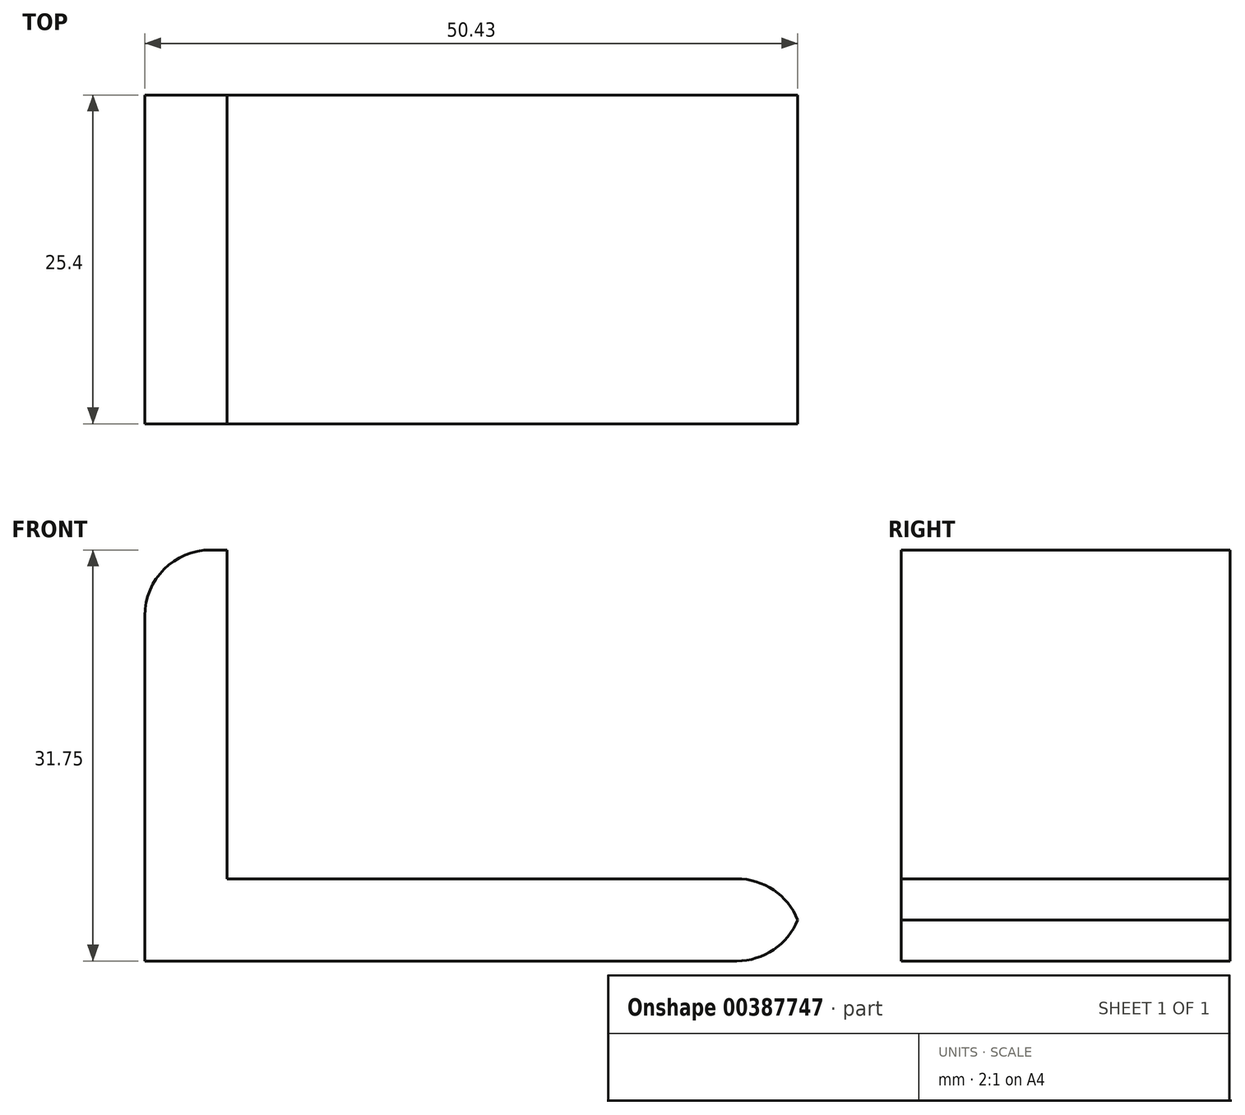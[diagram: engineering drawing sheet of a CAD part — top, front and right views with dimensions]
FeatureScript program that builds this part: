
annotation { "Feature Type Name" : "Feature", "Feature Type Description" : "" }
export const myFeature = defineFeature(function(context is Context, id is Id, definition is map)
    precondition{}
    {
        {
            var Q0;
            Q0=qCreatedBy(makeId("Front.planeOp"),FACE);
            var sketch = newSketch(context, id + "F0", { "sketchPlane" : qUnion([Q0])});
            skLineSegment(sketch, "E0.bottom", {"start": v(0, 0) * mm, "end": v(50.8, 0) * mm});
            skLineSegment(sketch, "E0.left", {"start": v(0, 0) * mm, "end": v(0, 31.75) * mm});
            skLineSegment(sketch, "E1", {"start": v(50.8, 0) * mm, "end": v(50.8, 6.35) * mm});
            skLineSegment(sketch, "E2", {"start": v(50.8, 6.35) * mm, "end": v(6.35, 6.35) * mm});
            skLineSegment(sketch, "E3", {"start": v(6.35, 6.35) * mm, "end": v(6.35, 31.75) * mm});
            skLineSegment(sketch, "E4", {"start": v(0, 31.75) * mm, "end": v(6.35, 31.75) * mm});
            skSolve(sketch);
        }
        {
            var Q0;
            Q0=makeQuery(id+"F0.imprint","IMPRINT",FACE,{"disambiguationData":[TD([[makeQuery(id+"F0.imprint","IMPRINT",EDGE,{"derivedFrom":sQuery(id+"F0.wireOp",EDGE,"E0.bottom")}),1.0]])]});
            extrude(context, id + "F1", {"entities" : qUnion([Q0]), "oppositeDirection" : true, "depth" : 25.4 * mm});
        }
        {
            var Q0;
            Q0=makeQuery(id+"F1.opExtrude","SWEPT_EDGE",EDGE,{"disambiguationData":[OSD([sQuery(id+"F0.wireOp",EDGE,"E1"),sQuery(id+"F0.wireOp",EDGE,"E2")])]});
            var Q1;
            Q1=makeQuery(id+"F1.opExtrude","SWEPT_EDGE",EDGE,{"disambiguationData":[OSD([sQuery(id+"F0.wireOp",EDGE,"E0.bottom"),sQuery(id+"F0.wireOp",EDGE,"E1")])]});
            fillet(context, id + "F2", {"entities" : qUnion([Q0, Q1]), "radius" : 5.08 * mm, "tangentPropagation" : true, "allowEdgeOverflow" : false});
        }
        {
            var Q0;
            Q0=makeQuery(id+"F1.opExtrude","SWEPT_EDGE",EDGE,{"disambiguationData":[OSD([sQuery(id+"F0.wireOp",EDGE,"E0.left"),sQuery(id+"F0.wireOp",EDGE,"E4")])]});
            fillet(context, id + "F3", {"entities" : qUnion([Q0]), "radius" : 5.08 * mm, "tangentPropagation" : true, "allowEdgeOverflow" : false});
        }
    });
